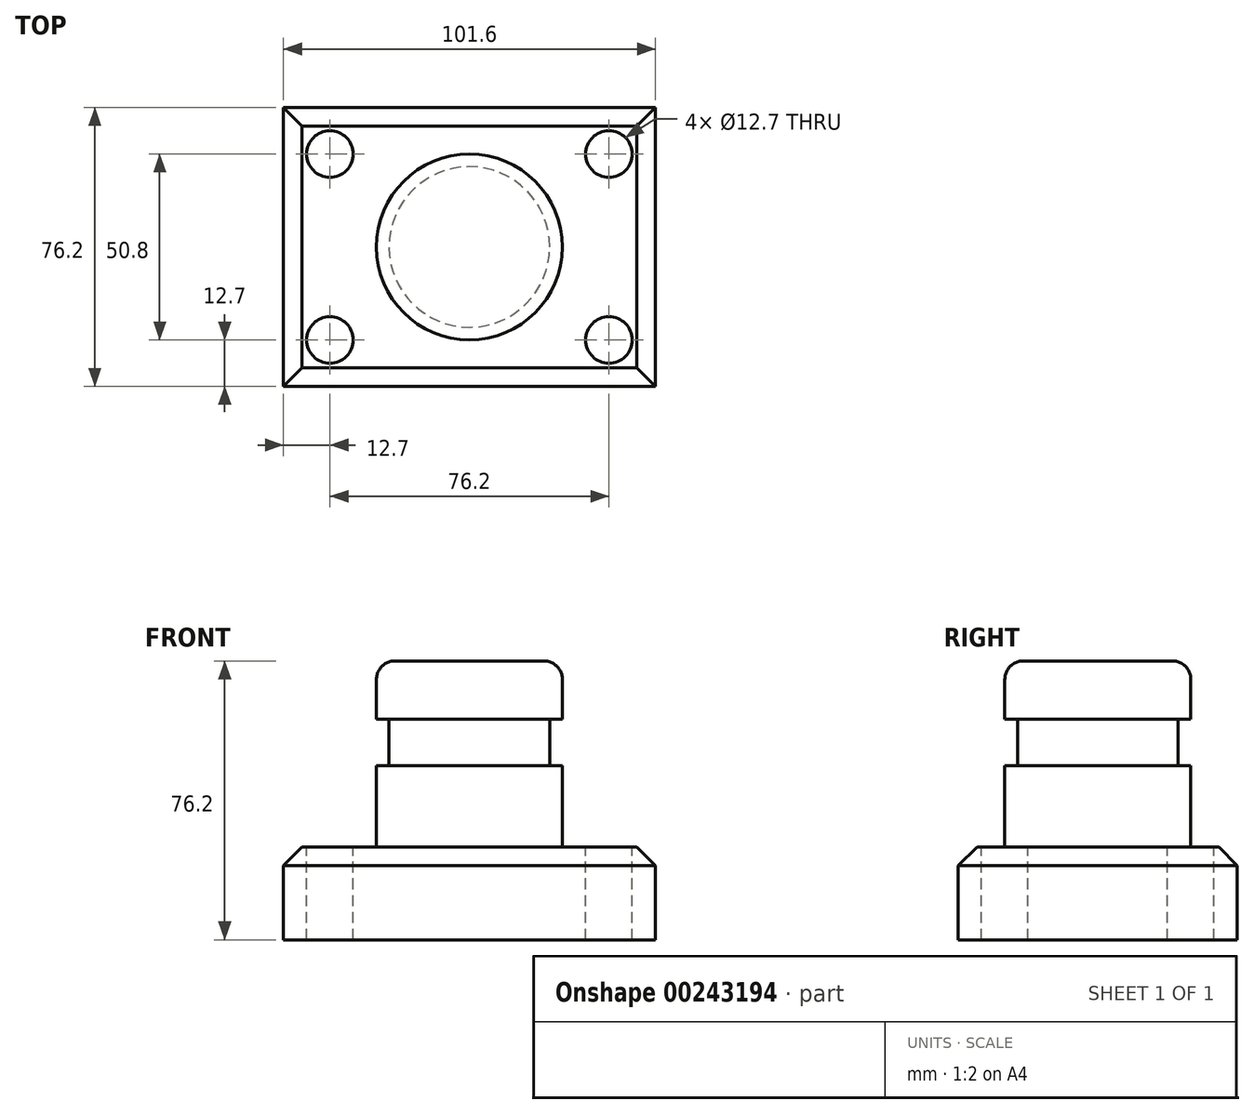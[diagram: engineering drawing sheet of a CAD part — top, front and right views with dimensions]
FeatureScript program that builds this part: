
annotation { "Feature Type Name" : "Feature", "Feature Type Description" : "" }
export const myFeature = defineFeature(function(context is Context, id is Id, definition is map)
    precondition{}
    {
        {
            var Q0;
            Q0=qCreatedBy(makeId("Top.planeOp"),FACE);
            var sketch = newSketch(context, id + "F0", { "sketchPlane" : qUnion([Q0])});
            skLineSegment(sketch, "E0.bottom", {"start": v(-50.8, 38.1) * mm, "end": v(50.8, 38.1) * mm});
            skLineSegment(sketch, "E0.top", {"start": v(-50.8, -38.1) * mm, "end": v(50.8, -38.1) * mm});
            skLineSegment(sketch, "E0.left", {"start": v(-50.8, 38.1) * mm, "end": v(-50.8, -38.1) * mm});
            skLineSegment(sketch, "E0.right", {"start": v(50.8, 38.1) * mm, "end": v(50.8, -38.1) * mm});
            skPoint(sketch, "E0.middle", {"position": v(0, 0) * mm});
            skSolve(sketch);
        }
        {
            var Q0;
            Q0=makeQuery(id+"F0.imprint","IMPRINT",FACE,{"disambiguationData":[TD([[makeQuery(id+"F0.imprint","IMPRINT",EDGE,{"derivedFrom":sQuery(id+"F0.wireOp",EDGE,"E0.bottom")}),-1.0]])]});
            extrude(context, id + "F1", {"entities" : qUnion([Q0]), "depth" : 25.4 * mm});
        }
        {
            var Q0;
            Q0=makeQuery(id+"F1.opExtrude","CAP_FACE",FACE,{"disambiguationData":[OSD([sQuery(id+"F0.wireOp",EDGE,"E0.bottom"),sQuery(id+"F0.wireOp",EDGE,"E0.top"),sQuery(id+"F0.wireOp",EDGE,"E0.left"),sQuery(id+"F0.wireOp",EDGE,"E0.right")])],"isStart":false});
            var sketch = newSketch(context, id + "F2", { "sketchPlane" : qUnion([Q0])});
            skCircle(sketch, "E1", {"center": v(-38.1, -25.4) * mm, "radius": 6.35 * mm});
            skCircle(sketch, "E2", {"center": v(-38.1, 25.4) * mm, "radius": 6.35 * mm});
            skCircle(sketch, "E3", {"center": v(38.1, -25.4) * mm, "radius": 6.35 * mm});
            skCircle(sketch, "E4", {"center": v(38.1, 25.4) * mm, "radius": 6.35 * mm});
            skSolve(sketch);
        }
        {
            var Q0;
            Q0=makeQuery(id+"F2.imprint","IMPRINT",FACE,{"disambiguationData":[TD([[makeQuery(id+"F2.imprint","IMPRINT",EDGE,{"derivedFrom":sQuery(id+"F2.wireOp",EDGE,"E2")}),1.0]])]});
            var Q1;
            Q1=makeQuery(id+"F2.imprint","IMPRINT",FACE,{"disambiguationData":[TD([[makeQuery(id+"F2.imprint","IMPRINT",EDGE,{"derivedFrom":sQuery(id+"F2.wireOp",EDGE,"E4")}),1.0]])]});
            var Q2;
            Q2=makeQuery(id+"F2.imprint","IMPRINT",FACE,{"disambiguationData":[TD([[makeQuery(id+"F2.imprint","IMPRINT",EDGE,{"derivedFrom":sQuery(id+"F2.wireOp",EDGE,"E3")}),1.0]])]});
            var Q3;
            Q3=makeQuery(id+"F2.imprint","IMPRINT",FACE,{"disambiguationData":[TD([[makeQuery(id+"F2.imprint","IMPRINT",EDGE,{"derivedFrom":sQuery(id+"F2.wireOp",EDGE,"E1")}),1.0]])]});
            extrude(context, id + "F3", {"entities" : qUnion([Q0, Q1, Q2, Q3]), "operationType" : NewBodyOperationType.REMOVE, "oppositeDirection" : true, "depth" : 25.4 * mm});
        }
        {
            var Q0;
            Q0=qCreatedBy(makeId("Front.planeOp"),FACE);
            var sketch = newSketch(context, id + "F4", { "sketchPlane" : qUnion([Q0])});
            skLineSegment(sketch, "E5.bottom", {"start": v(0, 0) * mm, "end": v(0, 0) * mm});
            skLineSegment(sketch, "E6.bottom", {"start": v(0, 25.4) * mm, "end": v(-25.4, 25.4) * mm});
            skLineSegment(sketch, "E6.top", {"start": v(0, 76.2) * mm, "end": v(-25.4, 76.2) * mm});
            skLineSegment(sketch, "E6.left", {"start": v(0, 25.4) * mm, "end": v(0, 76.2) * mm});
            skLineSegment(sketch, "E6.right", {"start": v(-25.4, 25.4) * mm, "end": v(-25.4, 76.2) * mm});
            skSolve(sketch);
        }
        {
            var Q0;
            Q0=makeQuery(id+"F4.imprint","IMPRINT",FACE,{"disambiguationData":[TD([[makeQuery(id+"F4.imprint","IMPRINT",EDGE,{"derivedFrom":sQuery(id+"F4.wireOp",EDGE,"E6.bottom")}),-1.0]])]});
            var Q1;
            Q1=sQuery(id+"F4.wireOp",EDGE,"E6.left");
            revolve(context, id + "F5", {"operationType" : NewBodyOperationType.ADD, "entities" : qUnion([Q0]), "axis" : qUnion([Q1]), "revolveType" : RevolveType.FULL});
        }
        {
            var Q0;
            Q0=qCreatedBy(makeId("Front.planeOp"),FACE);
            var sketch = newSketch(context, id + "F6", { "sketchPlane" : qUnion([Q0])});
            skLineSegment(sketch, "E7.bottom", {"start": v(-21.94, 60.28) * mm, "end": v(-38.1, 60.28) * mm});
            skLineSegment(sketch, "E7.top", {"start": v(-21.94, 47.58) * mm, "end": v(-38.1, 47.58) * mm});
            skLineSegment(sketch, "E7.left", {"start": v(-21.94, 60.28) * mm, "end": v(-21.94, 47.58) * mm});
            skLineSegment(sketch, "E7.right", {"start": v(-38.1, 60.28) * mm, "end": v(-38.1, 47.58) * mm});
            skSolve(sketch);
        }
        {
            var Q0;
            Q0=makeQuery(id+"F6.imprint","IMPRINT",FACE,{"disambiguationData":[TD([[makeQuery(id+"F6.imprint","IMPRINT",EDGE,{"derivedFrom":sQuery(id+"F6.wireOp",EDGE,"E7.bottom")}),1.0]])]});
            var Q1;
            Q1=makeQuery(id+"F5.opRevolve","SWEPT_FACE",FACE,{"disambiguationData":[OSD([sQuery(id+"F4.wireOp",EDGE,"E6.right")])]});
            revolve(context, id + "F7", {"operationType" : NewBodyOperationType.REMOVE, "entities" : qUnion([Q0]), "axis" : qUnion([Q1]), "revolveType" : RevolveType.FULL, "oppositeDirection" : true});
        }
        {
            var Q0;
            Q0=makeQuery(id+"F1.opExtrude","CAP_EDGE",EDGE,{"disambiguationData":[OSD([sQuery(id+"F0.wireOp",EDGE,"E0.top")])],"isStart":false});
            var Q1;
            Q1=makeQuery(id+"F1.opExtrude","CAP_EDGE",EDGE,{"disambiguationData":[OSD([sQuery(id+"F0.wireOp",EDGE,"E0.left")])],"isStart":false});
            var Q2;
            Q2=makeQuery(id+"F1.opExtrude","CAP_EDGE",EDGE,{"disambiguationData":[OSD([sQuery(id+"F0.wireOp",EDGE,"E0.bottom")])],"isStart":false});
            var Q3;
            Q3=makeQuery(id+"F1.opExtrude","CAP_EDGE",EDGE,{"disambiguationData":[OSD([sQuery(id+"F0.wireOp",EDGE,"E0.right")])],"isStart":false});
            chamfer(context, id + "F8", {"entities" : qUnion([Q0, Q1, Q2, Q3]), "width" : 5.08 * mm, "tangentPropagation" : true});
        }
        {
            var Q0;
            Q0=makeQuery(id+"F5.opRevolve","SWEPT_EDGE",EDGE,{"disambiguationData":[OSD([sQuery(id+"F4.wireOp",EDGE,"E6.bottom"),sQuery(id+"F4.wireOp",EDGE,"E6.right")])]});
            var Q1;
            Q1=makeQuery(id+"F5.opRevolve","SWEPT_EDGE",EDGE,{"disambiguationData":[OSD([sQuery(id+"F4.wireOp",EDGE,"E6.top"),sQuery(id+"F4.wireOp",EDGE,"E6.right")])]});
            fillet(context, id + "F9", {"entities" : qUnion([Q0, Q1]), "radius" : 5.08 * mm, "tangentPropagation" : true, "allowEdgeOverflow" : false});
        }
    });
